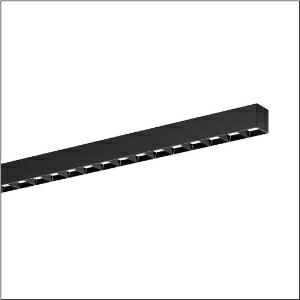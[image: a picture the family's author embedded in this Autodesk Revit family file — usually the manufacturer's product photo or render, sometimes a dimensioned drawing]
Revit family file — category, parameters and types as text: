
# Revit family: silica_21_51mx22tat4b
name_source: partatom
category: Lighting Fixtures
units: mm (PartAtom-declared; Revit-internal decimal feet)

## family parameters
Cut with Voids When Loaded = No
Host = Face
Light Source = No
Part Type = Normal
Room Calculation Point = No
Round Connector Dimension = Use Diameter
Shared = No

## types (1)
- --- (1 x LED, 3720 lm, 32.1 W, 6500K)
    Apparent Load = 32 VA
    CIE Flux Codes = 84 100 100 100 100
    Color Rendering = 80
    Color Temperature = 6500K
    Default Elevation = 1800 mm
    Description = Silica 21, office luminaire, primary light control with darklight reflector, of PMMA, black, CAT 2 (L<= 3000cd/m²), light emission: direct distribution, primary light characteristic: symmetric, installation type: surface-mounted, LED, rated luminous flux: 3.720lm, luminous efficacy: 110lm/W, light colour: 8tw, colour temperature: 2700..6500K, control gear: DALI DT8, with terminal, 3+2-pole, max. 2.5mm², mains connection: 220..240V, AC, 50/60Hz, rated input power: 33.8W, luminaire housing, of aluminium, matt jet black (RAL 9005), length: 1.204mm, width: 53mm, height: 53mm, protection rating (complete): IP20, insulation class (complete): insulation class I (protective earthing), certification: CE, permissible operating ambient temperature: 0..+35°C, standard: EN 50419, packaging unit: 1 piece
    Height = 53 mm
    Lamp = 1 x LED
    Lamp Light Flux = 3720 lm
    Lamp Power = 32.1 W
    Lamp count = 1
    Length = 1204 mm
    Luminous efficacy = 116 lm/W
    Manufacturer = Siteco
    ModVariant = No
    Model = 51MX22TAT4B
    Mounting Place = Ceiling
    Mounting Type = Surface mounted
    Number of Poles = 1
    OnlyDefault = Yes
    Power Factor = 1
    Product Name = Silica 21
    Product group = office luminaire | ceiling mounted
    ProductGroupID = 301
    Protection Class = Protection class I
    Protection Degree = IP 20
    RLX_Detail_Level = 1
    RLX_Emergency_Light_Flux = 0 lm
    RLX_Emergency_Type = 0
    RLX_Emergency_Type_DB = No
    RlxData = <blob elided: 40177 chars, md5=10adcb01>
    Socket = socket
    Standby Power = 0 W
    System Light Flux = 3720 lm
    System Power = 32 W
    Type Comments = individual setting
    Type Image = l_1335908.jpg
    URL = http://relux.com
    VarID = @adj_141193
    Voltage = 0 V
    Weight = 0.00 kg
    Width = 53 mm

## geometry (parser evidence)
native form markers: Blend x4, Sweep x9
no freeform markers — native parametric forms only
